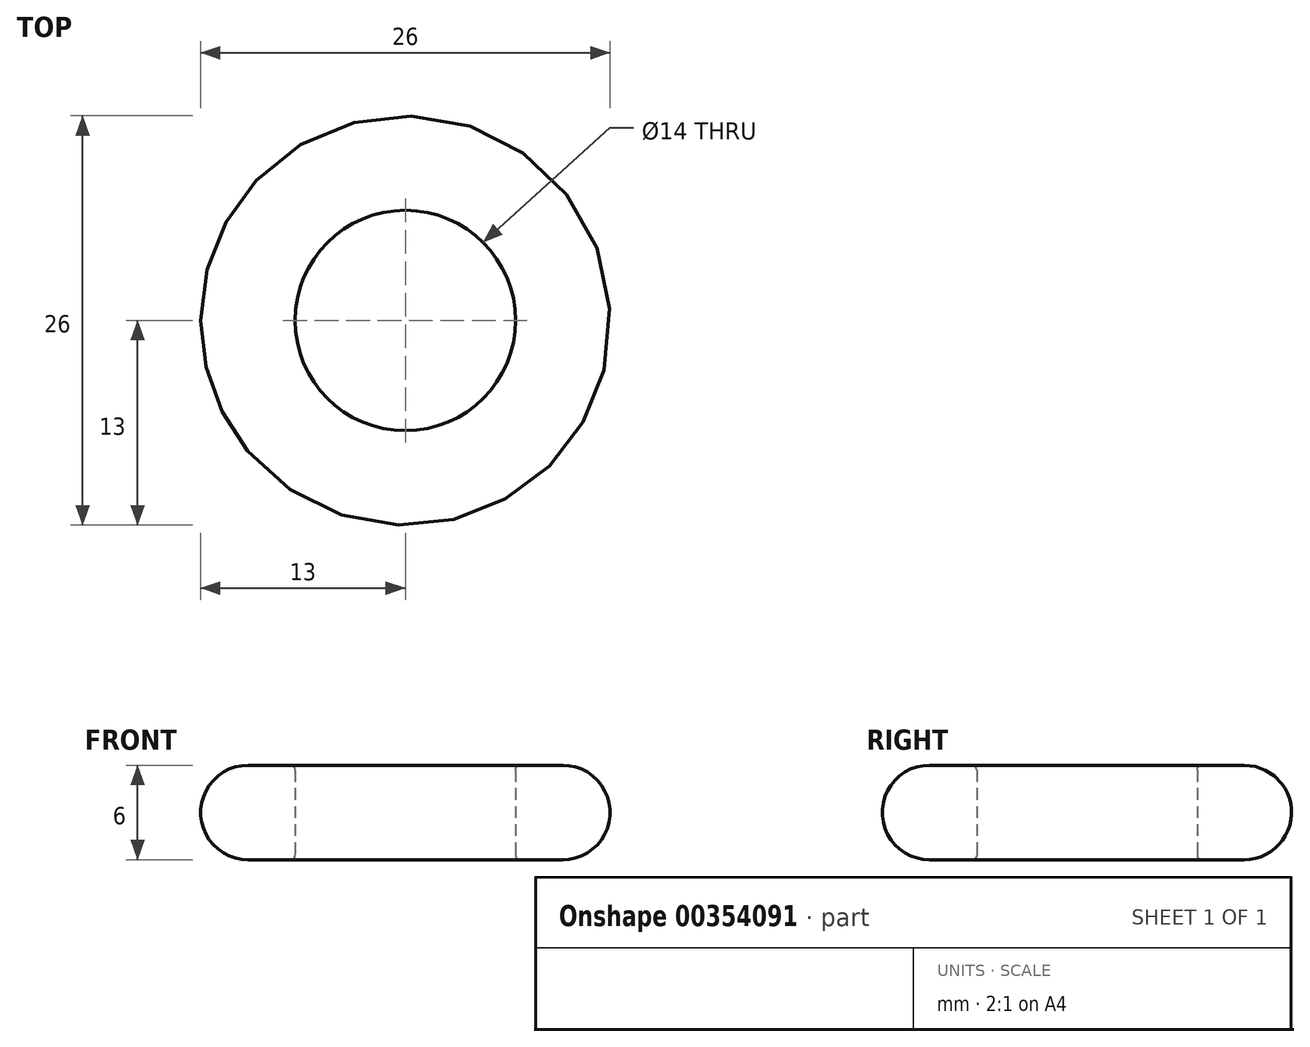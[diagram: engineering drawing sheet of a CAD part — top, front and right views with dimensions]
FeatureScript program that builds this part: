
annotation { "Feature Type Name" : "Feature", "Feature Type Description" : "" }
export const myFeature = defineFeature(function(context is Context, id is Id, definition is map)
    precondition{}
    {
        {
            var Q0;
            Q0=qCreatedBy(makeId("Front.planeOp"),FACE);
            var sketch = newSketch(context, id + "F0", { "sketchPlane" : qUnion([Q0])});
            skLineSegment(sketch, "E0", {"start": v(0, 0) * mm, "end": v(0, 6) * mm});
            skLineSegment(sketch, "E1", {"start": v(0, 6) * mm, "end": v(-3, 6) * mm});
            skLineSegment(sketch, "E2", {"start": v(0, 0) * mm, "end": v(-3, 0) * mm});
            skArc(sketch, "E3", {"start": v(-3, 6) * mm, "mid": v(-6, 3) * mm, "end": v(-3, 0) * mm});
            skLineSegment(sketch, "E4", {"start": v(0, 0) * mm, "end": v(7, 0) * mm});
            skLineSegment(sketch, "E5", {"start": v(7, 0) * mm, "end": v(7, 7.62) * mm});
            skSolve(sketch);
        }
        {
            var Q0;
            Q0=makeQuery(id+"F0.imprint","IMPRINT",FACE,{"disambiguationData":[TD([[makeQuery(id+"F0.imprint","IMPRINT",EDGE,{"derivedFrom":sQuery(id+"F0.wireOp",EDGE,"E0")}),1.0]])]});
            var Q1;
            Q1=sQuery(id+"F0.wireOp",EDGE,"E5");
            revolve(context, id + "F1", {"entities" : qUnion([Q0]), "axis" : qUnion([Q1]), "revolveType" : RevolveType.FULL});
        }
        {
            var Q0;
            Q0=makeQuery(id+"F1.opRevolve","SWEPT_EDGE",EDGE,{"disambiguationData":[OSD([sQuery(id+"F0.wireOp",EDGE,"E0"),sQuery(id+"F0.wireOp",EDGE,"E1")])]});
            var Q1;
            Q1=makeQuery(id+"F1.opRevolve","SWEPT_EDGE",EDGE,{"disambiguationData":[OSD([sQuery(id+"F0.wireOp",EDGE,"E0"),sQuery(id+"F0.wireOp",EDGE,"E2")])]});
            var Q2;
            Q2=makeQuery(id+"F1.opRevolve","SWEPT_EDGE",EDGE,{"disambiguationData":[OSD([sQuery(id+"F0.wireOp",EDGE,"E1"),sQuery(id+"F0.wireOp",EDGE,"E3")])]});
            var Q3;
            Q3=makeQuery(id+"F1.opRevolve","SWEPT_EDGE",EDGE,{"disambiguationData":[OSD([sQuery(id+"F0.wireOp",EDGE,"E2"),sQuery(id+"F0.wireOp",EDGE,"E3")])]});
            fillet(context, id + "F2", {"entities" : qUnion([Q0, Q1, Q2, Q3]), "radius" : 0.3 * mm, "tangentPropagation" : true, "allowEdgeOverflow" : false});
        }
    });
